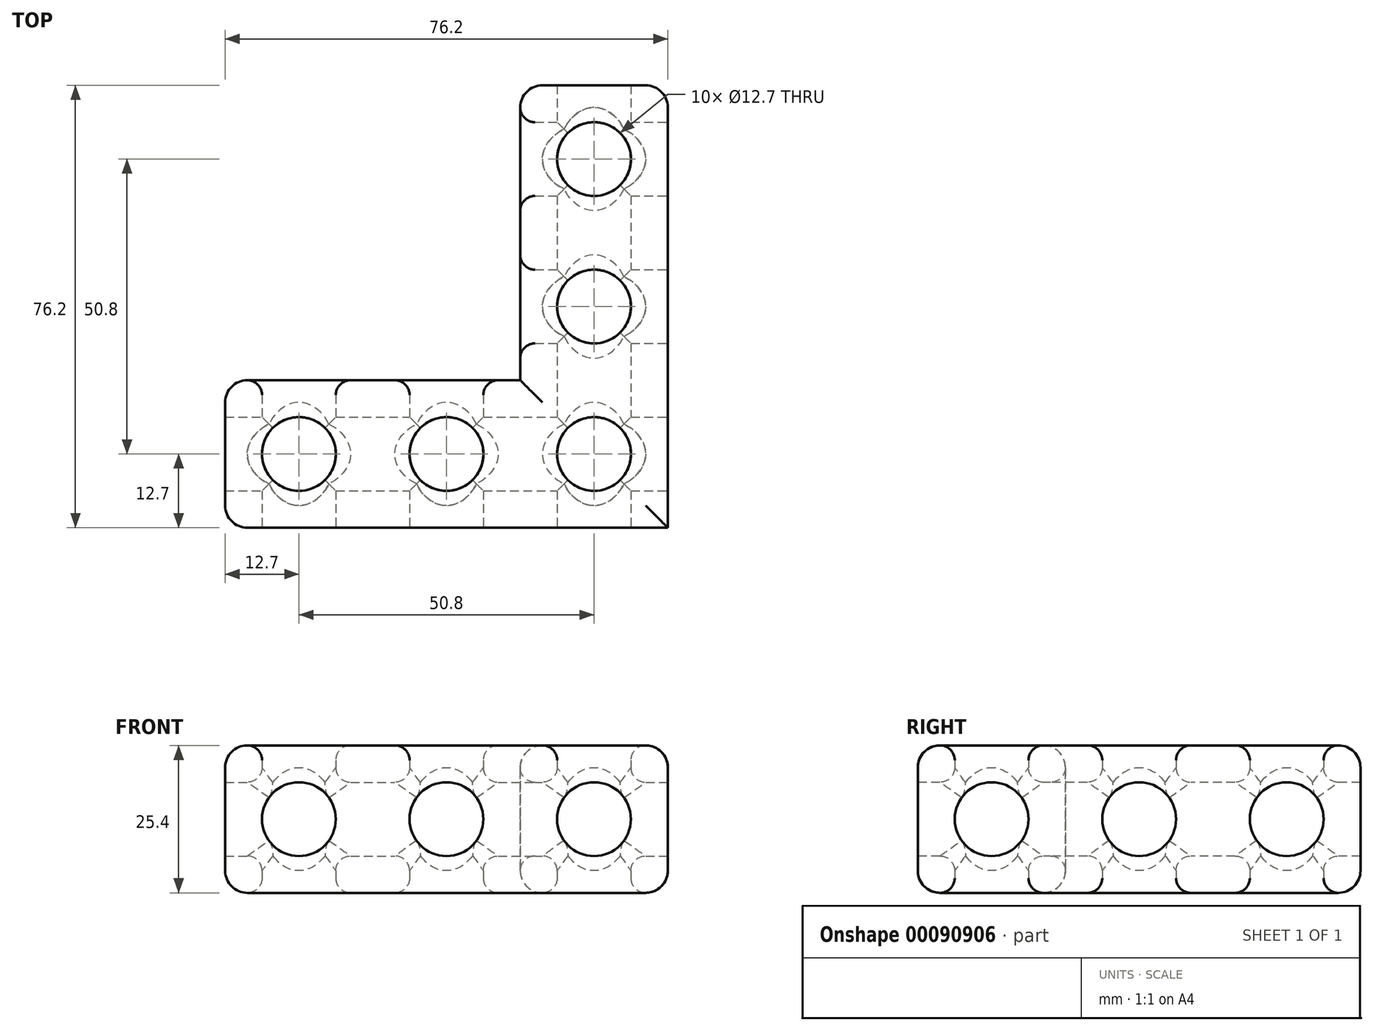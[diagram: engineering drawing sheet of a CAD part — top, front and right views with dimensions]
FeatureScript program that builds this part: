
annotation { "Feature Type Name" : "Feature", "Feature Type Description" : "" }
export const myFeature = defineFeature(function(context is Context, id is Id, definition is map)
    precondition{}
    {
        {
            var Q0;
            Q0=qCreatedBy(makeId("Top.planeOp"),FACE);
            var sketch = newSketch(context, id + "F0", { "sketchPlane" : qUnion([Q0])});
            skLineSegment(sketch, "E0.bottom", {"start": v(0, 0) * mm, "end": v(76.2, 0) * mm});
            skLineSegment(sketch, "E0.left", {"start": v(0, 0) * mm, "end": v(0, 25.4) * mm});
            skLineSegment(sketch, "E0.right", {"start": v(76.2, 0) * mm, "end": v(76.2, 18.8) * mm});
            skLineSegment(sketch, "E1.bottom", {"start": v(76.2, 0) * mm, "end": v(57.4, 0) * mm});
            skLineSegment(sketch, "E1.top", {"start": v(76.2, 76.2) * mm, "end": v(50.8, 76.2) * mm});
            skLineSegment(sketch, "E1.left", {"start": v(76.2, 0) * mm, "end": v(76.2, 76.2) * mm});
            skLineSegment(sketch, "E2", {"start": v(50.8, 76.2) * mm, "end": v(50.8, 25.4) * mm});
            skLineSegment(sketch, "E3", {"start": v(0, 25.4) * mm, "end": v(50.8, 25.4) * mm});
            skCircle(sketch, "E4", {"center": v(12.7, 12.7) * mm, "radius": 6.35 * mm});
            skCircle(sketch, "E5", {"center": v(38.1, 12.7) * mm, "radius": 6.35 * mm});
            skCircle(sketch, "E6", {"center": v(63.5, 12.7) * mm, "radius": 6.35 * mm});
            skCircle(sketch, "E7", {"center": v(63.5, 38.1) * mm, "radius": 6.35 * mm});
            skCircle(sketch, "E8", {"center": v(63.5, 63.5) * mm, "radius": 6.35 * mm});
            skSolve(sketch);
        }
        {
            var Q0;
            Q0 = qSketchRegion(id + "F0", true);
            extrude(context, id + "F1", {"entities" : qUnion([Q0]), "depth" : 25.4 * mm});
        }
        {
            var Q0;
            Q0=makeQuery(id+"F1.opExtrude","SWEPT_FACE",FACE,{"disambiguationData":[OSD([sQuery(id+"F0.wireOp",EDGE,"E0.bottom"),sQuery(id+"F0.wireOp",EDGE,"E1.bottom")])]});
            var sketch = newSketch(context, id + "F2", { "sketchPlane" : qUnion([Q0])});
            skCircle(sketch, "E9", {"center": v(12.7, 12.7) * mm, "radius": 6.35 * mm});
            skCircle(sketch, "E10", {"center": v(38.1, 12.7) * mm, "radius": 6.35 * mm});
            skCircle(sketch, "E11", {"center": v(63.5, 12.7) * mm, "radius": 6.35 * mm});
            skSolve(sketch);
        }
        {
            var Q0;
            Q0 = qSketchRegion(id + "F2", true);
            extrude(context, id + "F3", {"entities" : qUnion([Q0]), "operationType" : NewBodyOperationType.REMOVE, "oppositeDirection" : true, "depth" : 76.2 * mm});
        }
        {
            var Q0;
            Q0=makeQuery(id+"F1.opExtrude","SWEPT_FACE",FACE,{"disambiguationData":[OSD([sQuery(id+"F0.wireOp",EDGE,"E1.left")])]});
            var sketch = newSketch(context, id + "F4", { "sketchPlane" : qUnion([Q0])});
            skLineSegment(sketch, "E12.bottom", {"start": v(0, 0) * mm, "end": v(25.4, 0) * mm});
            skLineSegment(sketch, "E12.top", {"start": v(0, 25.4) * mm, "end": v(25.4, 25.4) * mm});
            skLineSegment(sketch, "E12.left", {"start": v(0, 0) * mm, "end": v(0, 25.4) * mm});
            skLineSegment(sketch, "E13.bottom", {"start": v(25.4, 0) * mm, "end": v(50.8, 0) * mm});
            skLineSegment(sketch, "E13.top", {"start": v(25.4, 25.4) * mm, "end": v(50.8, 25.4) * mm});
            skLineSegment(sketch, "E14.bottom", {"start": v(50.8, 0) * mm, "end": v(76.2, 0) * mm});
            skLineSegment(sketch, "E14.top", {"start": v(50.8, 25.4) * mm, "end": v(76.2, 25.4) * mm});
            skLineSegment(sketch, "E14.right", {"start": v(76.2, 0) * mm, "end": v(76.2, 25.4) * mm});
            skCircle(sketch, "E15", {"center": v(12.7, 12.7) * mm, "radius": 6.35 * mm});
            skCircle(sketch, "E16", {"center": v(38.1, 12.7) * mm, "radius": 6.35 * mm});
            skCircle(sketch, "E17", {"center": v(63.5, 12.7) * mm, "radius": 6.35 * mm});
            skSolve(sketch);
        }
        {
            var Q0;
            Q0=makeQuery(id+"F4.imprint","IMPRINT",FACE,{"disambiguationData":[TD([[makeQuery(id+"F4.imprint","IMPRINT",EDGE,{"derivedFrom":sQuery(id+"F4.wireOp",EDGE,"E15")}),1.0]])]});
            var Q1;
            Q1=makeQuery(id+"F4.imprint","IMPRINT",FACE,{"disambiguationData":[TD([[makeQuery(id+"F4.imprint","IMPRINT",EDGE,{"derivedFrom":sQuery(id+"F4.wireOp",EDGE,"E16")}),1.0]])]});
            var Q2;
            Q2=makeQuery(id+"F4.imprint","IMPRINT",FACE,{"disambiguationData":[TD([[makeQuery(id+"F4.imprint","IMPRINT",EDGE,{"derivedFrom":sQuery(id+"F4.wireOp",EDGE,"E17")}),1.0]])]});
            extrude(context, id + "F5", {"entities" : qUnion([Q0, Q1, Q2]), "operationType" : NewBodyOperationType.REMOVE, "oppositeDirection" : true, "depth" : 76.2 * mm});
        }
        {
            var Q0;
            Q0=makeQuery(id+"F1.opExtrude","CAP_EDGE",EDGE,{"disambiguationData":[OSD([sQuery(id+"F0.wireOp",EDGE,"E0.bottom"),sQuery(id+"F0.wireOp",EDGE,"E1.bottom")])],"isStart":false});
            var Q1;
            Q1=makeQuery(id+"F1.opExtrude","CAP_EDGE",EDGE,{"disambiguationData":[OSD([sQuery(id+"F0.wireOp",EDGE,"E1.left")])],"isStart":false});
            var Q2;
            Q2=makeQuery(id+"F1.opExtrude","CAP_EDGE",EDGE,{"disambiguationData":[OSD([sQuery(id+"F0.wireOp",EDGE,"E3")])],"isStart":false});
            var Q3;
            Q3=makeQuery(id+"F1.opExtrude","CAP_EDGE",EDGE,{"disambiguationData":[OSD([sQuery(id+"F0.wireOp",EDGE,"E2")])],"isStart":false});
            var Q4;
            Q4=makeQuery(id+"F1.opExtrude","SWEPT_EDGE",EDGE,{"disambiguationData":[OSD([sQuery(id+"F0.wireOp",EDGE,"E0.bottom"),sQuery(id+"F0.wireOp",EDGE,"E0.left")])]});
            var Q5;
            Q5=makeQuery(id+"F1.opExtrude","CAP_EDGE",EDGE,{"disambiguationData":[OSD([sQuery(id+"F0.wireOp",EDGE,"E0.bottom"),sQuery(id+"F0.wireOp",EDGE,"E1.bottom")])],"isStart":true});
            var Q6;
            Q6=makeQuery(id+"F1.opExtrude","CAP_EDGE",EDGE,{"disambiguationData":[OSD([sQuery(id+"F0.wireOp",EDGE,"E1.left")])],"isStart":true});
            var Q7;
            Q7=makeQuery(id+"F1.opExtrude","SWEPT_EDGE",EDGE,{"disambiguationData":[OSD([sQuery(id+"F0.wireOp",EDGE,"E1.bottom"),sQuery(id+"F0.wireOp",EDGE,"E1.left")])]});
            var Q8;
            Q8=makeQuery(id+"F1.opExtrude","CAP_EDGE",EDGE,{"disambiguationData":[OSD([sQuery(id+"F0.wireOp",EDGE,"E0.left")])],"isStart":false});
            var Q9;
            Q9=makeQuery(id+"F1.opExtrude","CAP_EDGE",EDGE,{"disambiguationData":[OSD([sQuery(id+"F0.wireOp",EDGE,"E0.left")])],"isStart":true});
            var Q10;
            Q10=makeQuery(id+"F1.opExtrude","SWEPT_EDGE",EDGE,{"disambiguationData":[OSD([sQuery(id+"F0.wireOp",EDGE,"E0.left"),sQuery(id+"F0.wireOp",EDGE,"E3")])]});
            var Q11;
            Q11=makeQuery(id+"F1.opExtrude","CAP_EDGE",EDGE,{"disambiguationData":[OSD([sQuery(id+"F0.wireOp",EDGE,"E3")])],"isStart":true});
            var Q12;
            Q12=makeQuery(id+"F1.opExtrude","SWEPT_EDGE",EDGE,{"disambiguationData":[OSD([sQuery(id+"F0.wireOp",EDGE,"E1.top"),sQuery(id+"F0.wireOp",EDGE,"E2")])]});
            var Q13;
            Q13=makeQuery(id+"F1.opExtrude","CAP_EDGE",EDGE,{"disambiguationData":[OSD([sQuery(id+"F0.wireOp",EDGE,"E2")])],"isStart":true});
            var Q14;
            Q14=makeQuery(id+"F1.opExtrude","CAP_EDGE",EDGE,{"disambiguationData":[OSD([sQuery(id+"F0.wireOp",EDGE,"E1.top")])],"isStart":true});
            var Q15;
            Q15=makeQuery(id+"F1.opExtrude","SWEPT_EDGE",EDGE,{"disambiguationData":[OSD([sQuery(id+"F0.wireOp",EDGE,"E1.top"),sQuery(id+"F0.wireOp",EDGE,"E1.left")])]});
            var Q16;
            Q16=makeQuery(id+"F1.opExtrude","CAP_EDGE",EDGE,{"disambiguationData":[OSD([sQuery(id+"F0.wireOp",EDGE,"E1.top")])],"isStart":false});
            fillet(context, id + "F6", {"entities" : qUnion([Q0, Q1, Q2, Q3, Q4, Q5, Q6, Q7, Q8, Q9, Q10, Q11, Q12, Q13, Q14, Q15, Q16]), "radius" : 3.8 * mm, "allowEdgeOverflow" : false});
        }
        {
            var Q0;
            {var subQ0=sQuery(id+"F0.wireOp",EDGE,"E4");var subQ1=makeQuery(id+"F1.opExtrude","SWEPT_FACE",FACE,{"disambiguationData":[OSD([subQ0])]});Q0=makeQuery(id+"F5.boolean.opBoolean","INTERSECT",EDGE,{"disambiguationData":[OD(0.0)],"derivedFrom":[makeQuery(id+"F3.boolean.opBoolean","SPLIT",FACE,{"disambiguationData":[TD([makeQuery(id+"F1.opExtrude","CAP_FACE",FACE,{"disambiguationData":[OSD([sQuery(id+"F0.wireOp",EDGE,"E0.bottom"),sQuery(id+"F0.wireOp",EDGE,"E0.left"),sQuery(id+"F0.wireOp",EDGE,"E1.bottom"),sQuery(id+"F0.wireOp",EDGE,"E1.top"),sQuery(id+"F0.wireOp",EDGE,"E1.left"),sQuery(id+"F0.wireOp",EDGE,"E2"),sQuery(id+"F0.wireOp",EDGE,"E3"),subQ0,sQuery(id+"F0.wireOp",EDGE,"E5"),sQuery(id+"F0.wireOp",EDGE,"E6"),sQuery(id+"F0.wireOp",EDGE,"E7"),sQuery(id+"F0.wireOp",EDGE,"E8")])],"isStart":true})])],"derivedFrom":subQ1}),makeQuery(id+"F5.opExtrude","SWEPT_FACE",FACE,{"disambiguationData":[OSD([sQuery(id+"F4.wireOp",EDGE,"E15")])]})]});}
            var Q1;
            Q1=makeQuery(id+"F3.boolean.opBoolean","INTERSECT",EDGE,{"disambiguationData":[OD(0.0)],"derivedFrom":[makeQuery(id+"F1.opExtrude","SWEPT_FACE",FACE,{"disambiguationData":[OSD([sQuery(id+"F0.wireOp",EDGE,"E4")])]}),makeQuery(id+"F3.opExtrude","SWEPT_FACE",FACE,{"disambiguationData":[OSD([sQuery(id+"F2.wireOp",EDGE,"E9")])]})]});
            var Q2;
            Q2=makeQuery(id+"F5.boolean.opBoolean","INTERSECT",EDGE,{"disambiguationData":[OD(0.0)],"derivedFrom":[makeQuery(id+"F3.boolean.opBoolean","COPY",FACE,{"disambiguationData":[OD(0.0)],"derivedFrom":makeQuery(id+"F3.opExtrude","SWEPT_FACE",FACE,{"disambiguationData":[OSD([sQuery(id+"F2.wireOp",EDGE,"E9")])]})}),makeQuery(id+"F5.opExtrude","SWEPT_FACE",FACE,{"disambiguationData":[OSD([sQuery(id+"F4.wireOp",EDGE,"E15")])]})]});
            var Q3;
            Q3=makeQuery(id+"F5.boolean.opBoolean","INTERSECT",EDGE,{"disambiguationData":[OD(0.0)],"derivedFrom":[makeQuery(id+"F3.boolean.opBoolean","COPY",FACE,{"disambiguationData":[OD(1.0)],"derivedFrom":makeQuery(id+"F3.opExtrude","SWEPT_FACE",FACE,{"disambiguationData":[OSD([sQuery(id+"F2.wireOp",EDGE,"E9")])]})}),makeQuery(id+"F5.opExtrude","SWEPT_FACE",FACE,{"disambiguationData":[OSD([sQuery(id+"F4.wireOp",EDGE,"E15")])]})]});
            var Q4;
            {var subQ0=sQuery(id+"F0.wireOp",EDGE,"E4");var subQ1=makeQuery(id+"F1.opExtrude","SWEPT_FACE",FACE,{"disambiguationData":[OSD([subQ0])]});Q4=makeQuery(id+"F5.boolean.opBoolean","INTERSECT",EDGE,{"disambiguationData":[OD(0.0)],"derivedFrom":[makeQuery(id+"F3.boolean.opBoolean","SPLIT",FACE,{"disambiguationData":[TD([makeQuery(id+"F1.opExtrude","CAP_FACE",FACE,{"disambiguationData":[OSD([sQuery(id+"F0.wireOp",EDGE,"E0.bottom"),sQuery(id+"F0.wireOp",EDGE,"E0.left"),sQuery(id+"F0.wireOp",EDGE,"E1.bottom"),sQuery(id+"F0.wireOp",EDGE,"E1.top"),sQuery(id+"F0.wireOp",EDGE,"E1.left"),sQuery(id+"F0.wireOp",EDGE,"E2"),sQuery(id+"F0.wireOp",EDGE,"E3"),subQ0,sQuery(id+"F0.wireOp",EDGE,"E5"),sQuery(id+"F0.wireOp",EDGE,"E6"),sQuery(id+"F0.wireOp",EDGE,"E7"),sQuery(id+"F0.wireOp",EDGE,"E8")])],"isStart":false})])],"derivedFrom":subQ1}),makeQuery(id+"F5.opExtrude","SWEPT_FACE",FACE,{"disambiguationData":[OSD([sQuery(id+"F4.wireOp",EDGE,"E15")])]})]});}
            var Q5;
            Q5=makeQuery(id+"F3.boolean.opBoolean","INTERSECT",EDGE,{"disambiguationData":[OD(3.0)],"derivedFrom":[makeQuery(id+"F1.opExtrude","SWEPT_FACE",FACE,{"disambiguationData":[OSD([sQuery(id+"F0.wireOp",EDGE,"E4")])]}),makeQuery(id+"F3.opExtrude","SWEPT_FACE",FACE,{"disambiguationData":[OSD([sQuery(id+"F2.wireOp",EDGE,"E9")])]})]});
            var Q6;
            Q6=makeQuery(id+"F3.boolean.opBoolean","INTERSECT",EDGE,{"disambiguationData":[OD(1.0)],"derivedFrom":[makeQuery(id+"F1.opExtrude","SWEPT_FACE",FACE,{"disambiguationData":[OSD([sQuery(id+"F0.wireOp",EDGE,"E4")])]}),makeQuery(id+"F3.opExtrude","SWEPT_FACE",FACE,{"disambiguationData":[OSD([sQuery(id+"F2.wireOp",EDGE,"E9")])]})]});
            var Q7;
            {var subQ0=sQuery(id+"F0.wireOp",EDGE,"E4");var subQ1=makeQuery(id+"F1.opExtrude","SWEPT_FACE",FACE,{"disambiguationData":[OSD([subQ0])]});Q7=makeQuery(id+"F5.boolean.opBoolean","INTERSECT",EDGE,{"disambiguationData":[OD(1.0)],"derivedFrom":[makeQuery(id+"F3.boolean.opBoolean","SPLIT",FACE,{"disambiguationData":[TD([makeQuery(id+"F1.opExtrude","CAP_FACE",FACE,{"disambiguationData":[OSD([sQuery(id+"F0.wireOp",EDGE,"E0.bottom"),sQuery(id+"F0.wireOp",EDGE,"E0.left"),sQuery(id+"F0.wireOp",EDGE,"E1.bottom"),sQuery(id+"F0.wireOp",EDGE,"E1.top"),sQuery(id+"F0.wireOp",EDGE,"E1.left"),sQuery(id+"F0.wireOp",EDGE,"E2"),sQuery(id+"F0.wireOp",EDGE,"E3"),subQ0,sQuery(id+"F0.wireOp",EDGE,"E5"),sQuery(id+"F0.wireOp",EDGE,"E6"),sQuery(id+"F0.wireOp",EDGE,"E7"),sQuery(id+"F0.wireOp",EDGE,"E8")])],"isStart":true})])],"derivedFrom":subQ1}),makeQuery(id+"F5.opExtrude","SWEPT_FACE",FACE,{"disambiguationData":[OSD([sQuery(id+"F4.wireOp",EDGE,"E15")])]})]});}
            var Q8;
            Q8=makeQuery(id+"F5.boolean.opBoolean","INTERSECT",EDGE,{"disambiguationData":[OD(1.0)],"derivedFrom":[makeQuery(id+"F3.boolean.opBoolean","COPY",FACE,{"disambiguationData":[OD(0.0)],"derivedFrom":makeQuery(id+"F3.opExtrude","SWEPT_FACE",FACE,{"disambiguationData":[OSD([sQuery(id+"F2.wireOp",EDGE,"E9")])]})}),makeQuery(id+"F5.opExtrude","SWEPT_FACE",FACE,{"disambiguationData":[OSD([sQuery(id+"F4.wireOp",EDGE,"E15")])]})]});
            var Q9;
            Q9=makeQuery(id+"F3.boolean.opBoolean","INTERSECT",EDGE,{"disambiguationData":[OD(2.0)],"derivedFrom":[makeQuery(id+"F1.opExtrude","SWEPT_FACE",FACE,{"disambiguationData":[OSD([sQuery(id+"F0.wireOp",EDGE,"E4")])]}),makeQuery(id+"F3.opExtrude","SWEPT_FACE",FACE,{"disambiguationData":[OSD([sQuery(id+"F2.wireOp",EDGE,"E9")])]})]});
            var Q10;
            {var subQ0=sQuery(id+"F0.wireOp",EDGE,"E4");var subQ1=makeQuery(id+"F1.opExtrude","SWEPT_FACE",FACE,{"disambiguationData":[OSD([subQ0])]});Q10=makeQuery(id+"F5.boolean.opBoolean","INTERSECT",EDGE,{"disambiguationData":[OD(1.0)],"derivedFrom":[makeQuery(id+"F3.boolean.opBoolean","SPLIT",FACE,{"disambiguationData":[TD([makeQuery(id+"F1.opExtrude","CAP_FACE",FACE,{"disambiguationData":[OSD([sQuery(id+"F0.wireOp",EDGE,"E0.bottom"),sQuery(id+"F0.wireOp",EDGE,"E0.left"),sQuery(id+"F0.wireOp",EDGE,"E1.bottom"),sQuery(id+"F0.wireOp",EDGE,"E1.top"),sQuery(id+"F0.wireOp",EDGE,"E1.left"),sQuery(id+"F0.wireOp",EDGE,"E2"),sQuery(id+"F0.wireOp",EDGE,"E3"),subQ0,sQuery(id+"F0.wireOp",EDGE,"E5"),sQuery(id+"F0.wireOp",EDGE,"E6"),sQuery(id+"F0.wireOp",EDGE,"E7"),sQuery(id+"F0.wireOp",EDGE,"E8")])],"isStart":false})])],"derivedFrom":subQ1}),makeQuery(id+"F5.opExtrude","SWEPT_FACE",FACE,{"disambiguationData":[OSD([sQuery(id+"F4.wireOp",EDGE,"E15")])]})]});}
            var Q11;
            Q11=makeQuery(id+"F5.boolean.opBoolean","INTERSECT",EDGE,{"disambiguationData":[OD(1.0)],"derivedFrom":[makeQuery(id+"F3.boolean.opBoolean","COPY",FACE,{"disambiguationData":[OD(1.0)],"derivedFrom":makeQuery(id+"F3.opExtrude","SWEPT_FACE",FACE,{"disambiguationData":[OSD([sQuery(id+"F2.wireOp",EDGE,"E9")])]})}),makeQuery(id+"F5.opExtrude","SWEPT_FACE",FACE,{"disambiguationData":[OSD([sQuery(id+"F4.wireOp",EDGE,"E15")])]})]});
            fillet(context, id + "F7", {"entities" : qUnion([Q0, Q1, Q2, Q3, Q4, Q5, Q6, Q7, Q8, Q9, Q10, Q11]), "radius" : 2.54 * mm, "tangentPropagation" : true, "allowEdgeOverflow" : false});
        }
        {
            var Q0;
            {var subQ0=sQuery(id+"F0.wireOp",EDGE,"E5");var subQ1=makeQuery(id+"F1.opExtrude","SWEPT_FACE",FACE,{"disambiguationData":[OSD([subQ0])]});Q0=makeQuery(id+"F5.boolean.opBoolean","INTERSECT",EDGE,{"disambiguationData":[OD(0.0)],"derivedFrom":[makeQuery(id+"F3.boolean.opBoolean","SPLIT",FACE,{"disambiguationData":[TD([makeQuery(id+"F1.opExtrude","CAP_FACE",FACE,{"disambiguationData":[OSD([sQuery(id+"F0.wireOp",EDGE,"E0.bottom"),sQuery(id+"F0.wireOp",EDGE,"E0.left"),sQuery(id+"F0.wireOp",EDGE,"E1.bottom"),sQuery(id+"F0.wireOp",EDGE,"E1.top"),sQuery(id+"F0.wireOp",EDGE,"E1.left"),sQuery(id+"F0.wireOp",EDGE,"E2"),sQuery(id+"F0.wireOp",EDGE,"E3"),sQuery(id+"F0.wireOp",EDGE,"E4"),subQ0,sQuery(id+"F0.wireOp",EDGE,"E6"),sQuery(id+"F0.wireOp",EDGE,"E7"),sQuery(id+"F0.wireOp",EDGE,"E8")])],"isStart":true})])],"derivedFrom":subQ1}),makeQuery(id+"F5.opExtrude","SWEPT_FACE",FACE,{"disambiguationData":[OSD([sQuery(id+"F4.wireOp",EDGE,"E15")])]})]});}
            var Q1;
            Q1=makeQuery(id+"F3.boolean.opBoolean","INTERSECT",EDGE,{"disambiguationData":[OD(0.0)],"derivedFrom":[makeQuery(id+"F1.opExtrude","SWEPT_FACE",FACE,{"disambiguationData":[OSD([sQuery(id+"F0.wireOp",EDGE,"E5")])]}),makeQuery(id+"F3.opExtrude","SWEPT_FACE",FACE,{"disambiguationData":[OSD([sQuery(id+"F2.wireOp",EDGE,"E10")])]})]});
            var Q2;
            Q2=makeQuery(id+"F3.boolean.opBoolean","INTERSECT",EDGE,{"disambiguationData":[OD(1.0)],"derivedFrom":[makeQuery(id+"F1.opExtrude","SWEPT_FACE",FACE,{"disambiguationData":[OSD([sQuery(id+"F0.wireOp",EDGE,"E5")])]}),makeQuery(id+"F3.opExtrude","SWEPT_FACE",FACE,{"disambiguationData":[OSD([sQuery(id+"F2.wireOp",EDGE,"E10")])]})]});
            var Q3;
            {var subQ0=sQuery(id+"F0.wireOp",EDGE,"E5");var subQ1=makeQuery(id+"F1.opExtrude","SWEPT_FACE",FACE,{"disambiguationData":[OSD([subQ0])]});Q3=makeQuery(id+"F5.boolean.opBoolean","INTERSECT",EDGE,{"disambiguationData":[OD(1.0)],"derivedFrom":[makeQuery(id+"F3.boolean.opBoolean","SPLIT",FACE,{"disambiguationData":[TD([makeQuery(id+"F1.opExtrude","CAP_FACE",FACE,{"disambiguationData":[OSD([sQuery(id+"F0.wireOp",EDGE,"E0.bottom"),sQuery(id+"F0.wireOp",EDGE,"E0.left"),sQuery(id+"F0.wireOp",EDGE,"E1.bottom"),sQuery(id+"F0.wireOp",EDGE,"E1.top"),sQuery(id+"F0.wireOp",EDGE,"E1.left"),sQuery(id+"F0.wireOp",EDGE,"E2"),sQuery(id+"F0.wireOp",EDGE,"E3"),sQuery(id+"F0.wireOp",EDGE,"E4"),subQ0,sQuery(id+"F0.wireOp",EDGE,"E6"),sQuery(id+"F0.wireOp",EDGE,"E7"),sQuery(id+"F0.wireOp",EDGE,"E8")])],"isStart":true})])],"derivedFrom":subQ1}),makeQuery(id+"F5.opExtrude","SWEPT_FACE",FACE,{"disambiguationData":[OSD([sQuery(id+"F4.wireOp",EDGE,"E15")])]})]});}
            var Q4;
            Q4=makeQuery(id+"F5.boolean.opBoolean","INTERSECT",EDGE,{"disambiguationData":[OD(0.0)],"derivedFrom":[makeQuery(id+"F3.boolean.opBoolean","COPY",FACE,{"disambiguationData":[OD(0.0)],"derivedFrom":makeQuery(id+"F3.opExtrude","SWEPT_FACE",FACE,{"disambiguationData":[OSD([sQuery(id+"F2.wireOp",EDGE,"E10")])]})}),makeQuery(id+"F5.opExtrude","SWEPT_FACE",FACE,{"disambiguationData":[OSD([sQuery(id+"F4.wireOp",EDGE,"E15")])]})]});
            var Q5;
            Q5=makeQuery(id+"F5.boolean.opBoolean","INTERSECT",EDGE,{"disambiguationData":[OD(0.0)],"derivedFrom":[makeQuery(id+"F3.boolean.opBoolean","COPY",FACE,{"disambiguationData":[OD(1.0)],"derivedFrom":makeQuery(id+"F3.opExtrude","SWEPT_FACE",FACE,{"disambiguationData":[OSD([sQuery(id+"F2.wireOp",EDGE,"E10")])]})}),makeQuery(id+"F5.opExtrude","SWEPT_FACE",FACE,{"disambiguationData":[OSD([sQuery(id+"F4.wireOp",EDGE,"E15")])]})]});
            var Q6;
            Q6=makeQuery(id+"F5.boolean.opBoolean","INTERSECT",EDGE,{"disambiguationData":[OD(1.0)],"derivedFrom":[makeQuery(id+"F3.boolean.opBoolean","COPY",FACE,{"disambiguationData":[OD(1.0)],"derivedFrom":makeQuery(id+"F3.opExtrude","SWEPT_FACE",FACE,{"disambiguationData":[OSD([sQuery(id+"F2.wireOp",EDGE,"E10")])]})}),makeQuery(id+"F5.opExtrude","SWEPT_FACE",FACE,{"disambiguationData":[OSD([sQuery(id+"F4.wireOp",EDGE,"E15")])]})]});
            var Q7;
            Q7=makeQuery(id+"F5.boolean.opBoolean","INTERSECT",EDGE,{"disambiguationData":[OD(1.0)],"derivedFrom":[makeQuery(id+"F3.boolean.opBoolean","COPY",FACE,{"disambiguationData":[OD(0.0)],"derivedFrom":makeQuery(id+"F3.opExtrude","SWEPT_FACE",FACE,{"disambiguationData":[OSD([sQuery(id+"F2.wireOp",EDGE,"E10")])]})}),makeQuery(id+"F5.opExtrude","SWEPT_FACE",FACE,{"disambiguationData":[OSD([sQuery(id+"F4.wireOp",EDGE,"E15")])]})]});
            var Q8;
            Q8=makeQuery(id+"F3.boolean.opBoolean","INTERSECT",EDGE,{"disambiguationData":[OD(2.0)],"derivedFrom":[makeQuery(id+"F1.opExtrude","SWEPT_FACE",FACE,{"disambiguationData":[OSD([sQuery(id+"F0.wireOp",EDGE,"E5")])]}),makeQuery(id+"F3.opExtrude","SWEPT_FACE",FACE,{"disambiguationData":[OSD([sQuery(id+"F2.wireOp",EDGE,"E10")])]})]});
            var Q9;
            {var subQ0=sQuery(id+"F0.wireOp",EDGE,"E5");var subQ1=makeQuery(id+"F1.opExtrude","SWEPT_FACE",FACE,{"disambiguationData":[OSD([subQ0])]});Q9=makeQuery(id+"F5.boolean.opBoolean","INTERSECT",EDGE,{"disambiguationData":[OD(0.0)],"derivedFrom":[makeQuery(id+"F3.boolean.opBoolean","SPLIT",FACE,{"disambiguationData":[TD([makeQuery(id+"F1.opExtrude","CAP_FACE",FACE,{"disambiguationData":[OSD([sQuery(id+"F0.wireOp",EDGE,"E0.bottom"),sQuery(id+"F0.wireOp",EDGE,"E0.left"),sQuery(id+"F0.wireOp",EDGE,"E1.bottom"),sQuery(id+"F0.wireOp",EDGE,"E1.top"),sQuery(id+"F0.wireOp",EDGE,"E1.left"),sQuery(id+"F0.wireOp",EDGE,"E2"),sQuery(id+"F0.wireOp",EDGE,"E3"),sQuery(id+"F0.wireOp",EDGE,"E4"),subQ0,sQuery(id+"F0.wireOp",EDGE,"E6"),sQuery(id+"F0.wireOp",EDGE,"E7"),sQuery(id+"F0.wireOp",EDGE,"E8")])],"isStart":false})])],"derivedFrom":subQ1}),makeQuery(id+"F5.opExtrude","SWEPT_FACE",FACE,{"disambiguationData":[OSD([sQuery(id+"F4.wireOp",EDGE,"E15")])]})]});}
            var Q10;
            Q10=makeQuery(id+"F3.boolean.opBoolean","INTERSECT",EDGE,{"disambiguationData":[OD(3.0)],"derivedFrom":[makeQuery(id+"F1.opExtrude","SWEPT_FACE",FACE,{"disambiguationData":[OSD([sQuery(id+"F0.wireOp",EDGE,"E5")])]}),makeQuery(id+"F3.opExtrude","SWEPT_FACE",FACE,{"disambiguationData":[OSD([sQuery(id+"F2.wireOp",EDGE,"E10")])]})]});
            var Q11;
            {var subQ0=sQuery(id+"F0.wireOp",EDGE,"E5");var subQ1=makeQuery(id+"F1.opExtrude","SWEPT_FACE",FACE,{"disambiguationData":[OSD([subQ0])]});Q11=makeQuery(id+"F5.boolean.opBoolean","INTERSECT",EDGE,{"disambiguationData":[OD(1.0)],"derivedFrom":[makeQuery(id+"F3.boolean.opBoolean","SPLIT",FACE,{"disambiguationData":[TD([makeQuery(id+"F1.opExtrude","CAP_FACE",FACE,{"disambiguationData":[OSD([sQuery(id+"F0.wireOp",EDGE,"E0.bottom"),sQuery(id+"F0.wireOp",EDGE,"E0.left"),sQuery(id+"F0.wireOp",EDGE,"E1.bottom"),sQuery(id+"F0.wireOp",EDGE,"E1.top"),sQuery(id+"F0.wireOp",EDGE,"E1.left"),sQuery(id+"F0.wireOp",EDGE,"E2"),sQuery(id+"F0.wireOp",EDGE,"E3"),sQuery(id+"F0.wireOp",EDGE,"E4"),subQ0,sQuery(id+"F0.wireOp",EDGE,"E6"),sQuery(id+"F0.wireOp",EDGE,"E7"),sQuery(id+"F0.wireOp",EDGE,"E8")])],"isStart":false})])],"derivedFrom":subQ1}),makeQuery(id+"F5.opExtrude","SWEPT_FACE",FACE,{"disambiguationData":[OSD([sQuery(id+"F4.wireOp",EDGE,"E15")])]})]});}
            var Q12;
            Q12=makeQuery(id+"F5.boolean.opBoolean","INTERSECT",EDGE,{"disambiguationData":[OD(1.0)],"derivedFrom":[makeQuery(id+"F3.boolean.opBoolean","COPY",FACE,{"disambiguationData":[OD(2.0)],"derivedFrom":makeQuery(id+"F3.opExtrude","SWEPT_FACE",FACE,{"disambiguationData":[OSD([sQuery(id+"F2.wireOp",EDGE,"E11")])]})}),makeQuery(id+"F5.opExtrude","SWEPT_FACE",FACE,{"disambiguationData":[OSD([sQuery(id+"F4.wireOp",EDGE,"E15")])]})]});
            var Q13;
            {var subQ0=sQuery(id+"F0.wireOp",EDGE,"E6");var subQ1=makeQuery(id+"F1.opExtrude","SWEPT_FACE",FACE,{"disambiguationData":[OSD([subQ0])]});Q13=makeQuery(id+"F5.boolean.opBoolean","INTERSECT",EDGE,{"disambiguationData":[OD(1.0)],"derivedFrom":[makeQuery(id+"F3.boolean.opBoolean","SPLIT",FACE,{"disambiguationData":[TD([makeQuery(id+"F1.opExtrude","CAP_FACE",FACE,{"disambiguationData":[OSD([sQuery(id+"F0.wireOp",EDGE,"E0.bottom"),sQuery(id+"F0.wireOp",EDGE,"E0.left"),sQuery(id+"F0.wireOp",EDGE,"E1.bottom"),sQuery(id+"F0.wireOp",EDGE,"E1.top"),sQuery(id+"F0.wireOp",EDGE,"E1.left"),sQuery(id+"F0.wireOp",EDGE,"E2"),sQuery(id+"F0.wireOp",EDGE,"E3"),sQuery(id+"F0.wireOp",EDGE,"E4"),sQuery(id+"F0.wireOp",EDGE,"E5"),subQ0,sQuery(id+"F0.wireOp",EDGE,"E7"),sQuery(id+"F0.wireOp",EDGE,"E8")])],"isStart":true})])],"derivedFrom":subQ1}),makeQuery(id+"F5.opExtrude","SWEPT_FACE",FACE,{"disambiguationData":[OSD([sQuery(id+"F4.wireOp",EDGE,"E15")])]})]});}
            var Q14;
            Q14=makeQuery(id+"F3.boolean.opBoolean","INTERSECT",EDGE,{"disambiguationData":[OD(2.0)],"derivedFrom":[makeQuery(id+"F1.opExtrude","SWEPT_FACE",FACE,{"disambiguationData":[OSD([sQuery(id+"F0.wireOp",EDGE,"E6")])]}),makeQuery(id+"F3.opExtrude","SWEPT_FACE",FACE,{"disambiguationData":[OSD([sQuery(id+"F2.wireOp",EDGE,"E11")])]})]});
            var Q15;
            {var subQ0=sQuery(id+"F0.wireOp",EDGE,"E6");var subQ1=makeQuery(id+"F1.opExtrude","SWEPT_FACE",FACE,{"disambiguationData":[OSD([subQ0])]});Q15=makeQuery(id+"F5.boolean.opBoolean","INTERSECT",EDGE,{"disambiguationData":[OD(1.0)],"derivedFrom":[makeQuery(id+"F3.boolean.opBoolean","SPLIT",FACE,{"disambiguationData":[TD([makeQuery(id+"F1.opExtrude","CAP_FACE",FACE,{"disambiguationData":[OSD([sQuery(id+"F0.wireOp",EDGE,"E0.bottom"),sQuery(id+"F0.wireOp",EDGE,"E0.left"),sQuery(id+"F0.wireOp",EDGE,"E1.bottom"),sQuery(id+"F0.wireOp",EDGE,"E1.top"),sQuery(id+"F0.wireOp",EDGE,"E1.left"),sQuery(id+"F0.wireOp",EDGE,"E2"),sQuery(id+"F0.wireOp",EDGE,"E3"),sQuery(id+"F0.wireOp",EDGE,"E4"),sQuery(id+"F0.wireOp",EDGE,"E5"),subQ0,sQuery(id+"F0.wireOp",EDGE,"E7"),sQuery(id+"F0.wireOp",EDGE,"E8")])],"isStart":false})])],"derivedFrom":subQ1}),makeQuery(id+"F5.opExtrude","SWEPT_FACE",FACE,{"disambiguationData":[OSD([sQuery(id+"F4.wireOp",EDGE,"E15")])]})]});}
            var Q16;
            Q16=makeQuery(id+"F3.boolean.opBoolean","INTERSECT",EDGE,{"disambiguationData":[OD(3.0)],"derivedFrom":[makeQuery(id+"F1.opExtrude","SWEPT_FACE",FACE,{"disambiguationData":[OSD([sQuery(id+"F0.wireOp",EDGE,"E6")])]}),makeQuery(id+"F3.opExtrude","SWEPT_FACE",FACE,{"disambiguationData":[OSD([sQuery(id+"F2.wireOp",EDGE,"E11")])]})]});
            var Q17;
            Q17=makeQuery(id+"F3.boolean.opBoolean","INTERSECT",EDGE,{"disambiguationData":[OD(0.0)],"derivedFrom":[makeQuery(id+"F1.opExtrude","SWEPT_FACE",FACE,{"disambiguationData":[OSD([sQuery(id+"F0.wireOp",EDGE,"E6")])]}),makeQuery(id+"F3.opExtrude","SWEPT_FACE",FACE,{"disambiguationData":[OSD([sQuery(id+"F2.wireOp",EDGE,"E11")])]})]});
            var Q18;
            Q18=makeQuery(id+"F5.boolean.opBoolean","INTERSECT",EDGE,{"disambiguationData":[OD(0.0)],"derivedFrom":[makeQuery(id+"F3.boolean.opBoolean","COPY",FACE,{"disambiguationData":[OD(0.0)],"derivedFrom":makeQuery(id+"F3.opExtrude","SWEPT_FACE",FACE,{"disambiguationData":[OSD([sQuery(id+"F2.wireOp",EDGE,"E11")])]})}),makeQuery(id+"F5.opExtrude","SWEPT_FACE",FACE,{"disambiguationData":[OSD([sQuery(id+"F4.wireOp",EDGE,"E15")])]})]});
            var Q19;
            Q19=makeQuery(id+"F3.boolean.opBoolean","INTERSECT",EDGE,{"disambiguationData":[OD(1.0)],"derivedFrom":[makeQuery(id+"F1.opExtrude","SWEPT_FACE",FACE,{"disambiguationData":[OSD([sQuery(id+"F0.wireOp",EDGE,"E6")])]}),makeQuery(id+"F3.opExtrude","SWEPT_FACE",FACE,{"disambiguationData":[OSD([sQuery(id+"F2.wireOp",EDGE,"E11")])]})]});
            var Q20;
            {var subQ0=sQuery(id+"F0.wireOp",EDGE,"E6");var subQ1=makeQuery(id+"F1.opExtrude","SWEPT_FACE",FACE,{"disambiguationData":[OSD([subQ0])]});Q20=makeQuery(id+"F5.boolean.opBoolean","INTERSECT",EDGE,{"disambiguationData":[OD(0.0)],"derivedFrom":[makeQuery(id+"F3.boolean.opBoolean","SPLIT",FACE,{"disambiguationData":[TD([makeQuery(id+"F1.opExtrude","CAP_FACE",FACE,{"disambiguationData":[OSD([sQuery(id+"F0.wireOp",EDGE,"E0.bottom"),sQuery(id+"F0.wireOp",EDGE,"E0.left"),sQuery(id+"F0.wireOp",EDGE,"E1.bottom"),sQuery(id+"F0.wireOp",EDGE,"E1.top"),sQuery(id+"F0.wireOp",EDGE,"E1.left"),sQuery(id+"F0.wireOp",EDGE,"E2"),sQuery(id+"F0.wireOp",EDGE,"E3"),sQuery(id+"F0.wireOp",EDGE,"E4"),sQuery(id+"F0.wireOp",EDGE,"E5"),subQ0,sQuery(id+"F0.wireOp",EDGE,"E7"),sQuery(id+"F0.wireOp",EDGE,"E8")])],"isStart":false})])],"derivedFrom":subQ1}),makeQuery(id+"F5.opExtrude","SWEPT_FACE",FACE,{"disambiguationData":[OSD([sQuery(id+"F4.wireOp",EDGE,"E15")])]})]});}
            var Q21;
            {var subQ0=sQuery(id+"F0.wireOp",EDGE,"E6");var subQ1=makeQuery(id+"F1.opExtrude","SWEPT_FACE",FACE,{"disambiguationData":[OSD([subQ0])]});Q21=makeQuery(id+"F5.boolean.opBoolean","INTERSECT",EDGE,{"disambiguationData":[OD(0.0)],"derivedFrom":[makeQuery(id+"F3.boolean.opBoolean","SPLIT",FACE,{"disambiguationData":[TD([makeQuery(id+"F1.opExtrude","CAP_FACE",FACE,{"disambiguationData":[OSD([sQuery(id+"F0.wireOp",EDGE,"E0.bottom"),sQuery(id+"F0.wireOp",EDGE,"E0.left"),sQuery(id+"F0.wireOp",EDGE,"E1.bottom"),sQuery(id+"F0.wireOp",EDGE,"E1.top"),sQuery(id+"F0.wireOp",EDGE,"E1.left"),sQuery(id+"F0.wireOp",EDGE,"E2"),sQuery(id+"F0.wireOp",EDGE,"E3"),sQuery(id+"F0.wireOp",EDGE,"E4"),sQuery(id+"F0.wireOp",EDGE,"E5"),subQ0,sQuery(id+"F0.wireOp",EDGE,"E7"),sQuery(id+"F0.wireOp",EDGE,"E8")])],"isStart":true})])],"derivedFrom":subQ1}),makeQuery(id+"F5.opExtrude","SWEPT_FACE",FACE,{"disambiguationData":[OSD([sQuery(id+"F4.wireOp",EDGE,"E15")])]})]});}
            var Q22;
            Q22=makeQuery(id+"F5.boolean.opBoolean","INTERSECT",EDGE,{"disambiguationData":[OD(0.0)],"derivedFrom":[makeQuery(id+"F3.boolean.opBoolean","COPY",FACE,{"disambiguationData":[OD(2.0)],"derivedFrom":makeQuery(id+"F3.opExtrude","SWEPT_FACE",FACE,{"disambiguationData":[OSD([sQuery(id+"F2.wireOp",EDGE,"E11")])]})}),makeQuery(id+"F5.opExtrude","SWEPT_FACE",FACE,{"disambiguationData":[OSD([sQuery(id+"F4.wireOp",EDGE,"E15")])]})]});
            var Q23;
            Q23=makeQuery(id+"F5.boolean.opBoolean","INTERSECT",EDGE,{"disambiguationData":[OD(1.0)],"derivedFrom":[makeQuery(id+"F3.boolean.opBoolean","COPY",FACE,{"disambiguationData":[OD(0.0)],"derivedFrom":makeQuery(id+"F3.opExtrude","SWEPT_FACE",FACE,{"disambiguationData":[OSD([sQuery(id+"F2.wireOp",EDGE,"E11")])]})}),makeQuery(id+"F5.opExtrude","SWEPT_FACE",FACE,{"disambiguationData":[OSD([sQuery(id+"F4.wireOp",EDGE,"E15")])]})]});
            var Q24;
            Q24=makeQuery(id+"F3.boolean.opBoolean","INTERSECT",EDGE,{"disambiguationData":[OD(0.0)],"derivedFrom":[makeQuery(id+"F1.opExtrude","SWEPT_FACE",FACE,{"disambiguationData":[OSD([sQuery(id+"F0.wireOp",EDGE,"E7")])]}),makeQuery(id+"F3.opExtrude","SWEPT_FACE",FACE,{"disambiguationData":[OSD([sQuery(id+"F2.wireOp",EDGE,"E11")])]})]});
            var Q25;
            {var subQ0=sQuery(id+"F0.wireOp",EDGE,"E7");var subQ1=makeQuery(id+"F1.opExtrude","SWEPT_FACE",FACE,{"disambiguationData":[OSD([subQ0])]});Q25=makeQuery(id+"F5.boolean.opBoolean","INTERSECT",EDGE,{"disambiguationData":[OD(0.0)],"derivedFrom":[makeQuery(id+"F3.boolean.opBoolean","SPLIT",FACE,{"disambiguationData":[TD([makeQuery(id+"F1.opExtrude","CAP_FACE",FACE,{"disambiguationData":[OSD([sQuery(id+"F0.wireOp",EDGE,"E0.bottom"),sQuery(id+"F0.wireOp",EDGE,"E0.left"),sQuery(id+"F0.wireOp",EDGE,"E1.bottom"),sQuery(id+"F0.wireOp",EDGE,"E1.top"),sQuery(id+"F0.wireOp",EDGE,"E1.left"),sQuery(id+"F0.wireOp",EDGE,"E2"),sQuery(id+"F0.wireOp",EDGE,"E3"),sQuery(id+"F0.wireOp",EDGE,"E4"),sQuery(id+"F0.wireOp",EDGE,"E5"),sQuery(id+"F0.wireOp",EDGE,"E6"),subQ0,sQuery(id+"F0.wireOp",EDGE,"E8")])],"isStart":true})])],"derivedFrom":subQ1}),makeQuery(id+"F5.opExtrude","SWEPT_FACE",FACE,{"disambiguationData":[OSD([sQuery(id+"F4.wireOp",EDGE,"E16")])]})]});}
            var Q26;
            Q26=makeQuery(id+"F5.boolean.opBoolean","INTERSECT",EDGE,{"disambiguationData":[OD(0.0)],"derivedFrom":[makeQuery(id+"F3.boolean.opBoolean","COPY",FACE,{"disambiguationData":[OD(2.0)],"derivedFrom":makeQuery(id+"F3.opExtrude","SWEPT_FACE",FACE,{"disambiguationData":[OSD([sQuery(id+"F2.wireOp",EDGE,"E11")])]})}),makeQuery(id+"F5.opExtrude","SWEPT_FACE",FACE,{"disambiguationData":[OSD([sQuery(id+"F4.wireOp",EDGE,"E16")])]})]});
            var Q27;
            Q27=makeQuery(id+"F3.boolean.opBoolean","INTERSECT",EDGE,{"disambiguationData":[OD(2.0)],"derivedFrom":[makeQuery(id+"F1.opExtrude","SWEPT_FACE",FACE,{"disambiguationData":[OSD([sQuery(id+"F0.wireOp",EDGE,"E7")])]}),makeQuery(id+"F3.opExtrude","SWEPT_FACE",FACE,{"disambiguationData":[OSD([sQuery(id+"F2.wireOp",EDGE,"E11")])]})]});
            var Q28;
            {var subQ0=sQuery(id+"F0.wireOp",EDGE,"E7");var subQ1=makeQuery(id+"F1.opExtrude","SWEPT_FACE",FACE,{"disambiguationData":[OSD([subQ0])]});Q28=makeQuery(id+"F5.boolean.opBoolean","INTERSECT",EDGE,{"disambiguationData":[OD(0.0)],"derivedFrom":[makeQuery(id+"F3.boolean.opBoolean","SPLIT",FACE,{"disambiguationData":[TD([makeQuery(id+"F1.opExtrude","CAP_FACE",FACE,{"disambiguationData":[OSD([sQuery(id+"F0.wireOp",EDGE,"E0.bottom"),sQuery(id+"F0.wireOp",EDGE,"E0.left"),sQuery(id+"F0.wireOp",EDGE,"E1.bottom"),sQuery(id+"F0.wireOp",EDGE,"E1.top"),sQuery(id+"F0.wireOp",EDGE,"E1.left"),sQuery(id+"F0.wireOp",EDGE,"E2"),sQuery(id+"F0.wireOp",EDGE,"E3"),sQuery(id+"F0.wireOp",EDGE,"E4"),sQuery(id+"F0.wireOp",EDGE,"E5"),sQuery(id+"F0.wireOp",EDGE,"E6"),subQ0,sQuery(id+"F0.wireOp",EDGE,"E8")])],"isStart":false})])],"derivedFrom":subQ1}),makeQuery(id+"F5.opExtrude","SWEPT_FACE",FACE,{"disambiguationData":[OSD([sQuery(id+"F4.wireOp",EDGE,"E16")])]})]});}
            var Q29;
            Q29=makeQuery(id+"F5.boolean.opBoolean","INTERSECT",EDGE,{"disambiguationData":[OD(1.0)],"derivedFrom":[makeQuery(id+"F3.boolean.opBoolean","COPY",FACE,{"disambiguationData":[OD(2.0)],"derivedFrom":makeQuery(id+"F3.opExtrude","SWEPT_FACE",FACE,{"disambiguationData":[OSD([sQuery(id+"F2.wireOp",EDGE,"E11")])]})}),makeQuery(id+"F5.opExtrude","SWEPT_FACE",FACE,{"disambiguationData":[OSD([sQuery(id+"F4.wireOp",EDGE,"E16")])]})]});
            var Q30;
            {var subQ0=sQuery(id+"F0.wireOp",EDGE,"E7");var subQ1=makeQuery(id+"F1.opExtrude","SWEPT_FACE",FACE,{"disambiguationData":[OSD([subQ0])]});Q30=makeQuery(id+"F5.boolean.opBoolean","INTERSECT",EDGE,{"disambiguationData":[OD(1.0)],"derivedFrom":[makeQuery(id+"F3.boolean.opBoolean","SPLIT",FACE,{"disambiguationData":[TD([makeQuery(id+"F1.opExtrude","CAP_FACE",FACE,{"disambiguationData":[OSD([sQuery(id+"F0.wireOp",EDGE,"E0.bottom"),sQuery(id+"F0.wireOp",EDGE,"E0.left"),sQuery(id+"F0.wireOp",EDGE,"E1.bottom"),sQuery(id+"F0.wireOp",EDGE,"E1.top"),sQuery(id+"F0.wireOp",EDGE,"E1.left"),sQuery(id+"F0.wireOp",EDGE,"E2"),sQuery(id+"F0.wireOp",EDGE,"E3"),sQuery(id+"F0.wireOp",EDGE,"E4"),sQuery(id+"F0.wireOp",EDGE,"E5"),sQuery(id+"F0.wireOp",EDGE,"E6"),subQ0,sQuery(id+"F0.wireOp",EDGE,"E8")])],"isStart":true})])],"derivedFrom":subQ1}),makeQuery(id+"F5.opExtrude","SWEPT_FACE",FACE,{"disambiguationData":[OSD([sQuery(id+"F4.wireOp",EDGE,"E16")])]})]});}
            var Q31;
            {var subQ0=sQuery(id+"F0.wireOp",EDGE,"E7");var subQ1=makeQuery(id+"F1.opExtrude","SWEPT_FACE",FACE,{"disambiguationData":[OSD([subQ0])]});Q31=makeQuery(id+"F5.boolean.opBoolean","INTERSECT",EDGE,{"disambiguationData":[OD(1.0)],"derivedFrom":[makeQuery(id+"F3.boolean.opBoolean","SPLIT",FACE,{"disambiguationData":[TD([makeQuery(id+"F1.opExtrude","CAP_FACE",FACE,{"disambiguationData":[OSD([sQuery(id+"F0.wireOp",EDGE,"E0.bottom"),sQuery(id+"F0.wireOp",EDGE,"E0.left"),sQuery(id+"F0.wireOp",EDGE,"E1.bottom"),sQuery(id+"F0.wireOp",EDGE,"E1.top"),sQuery(id+"F0.wireOp",EDGE,"E1.left"),sQuery(id+"F0.wireOp",EDGE,"E2"),sQuery(id+"F0.wireOp",EDGE,"E3"),sQuery(id+"F0.wireOp",EDGE,"E4"),sQuery(id+"F0.wireOp",EDGE,"E5"),sQuery(id+"F0.wireOp",EDGE,"E6"),subQ0,sQuery(id+"F0.wireOp",EDGE,"E8")])],"isStart":false})])],"derivedFrom":subQ1}),makeQuery(id+"F5.opExtrude","SWEPT_FACE",FACE,{"disambiguationData":[OSD([sQuery(id+"F4.wireOp",EDGE,"E16")])]})]});}
            var Q32;
            Q32=makeQuery(id+"F5.boolean.opBoolean","INTERSECT",EDGE,{"disambiguationData":[OD(1.0)],"derivedFrom":[makeQuery(id+"F3.boolean.opBoolean","COPY",FACE,{"disambiguationData":[OD(3.0)],"derivedFrom":makeQuery(id+"F3.opExtrude","SWEPT_FACE",FACE,{"disambiguationData":[OSD([sQuery(id+"F2.wireOp",EDGE,"E11")])]})}),makeQuery(id+"F5.opExtrude","SWEPT_FACE",FACE,{"disambiguationData":[OSD([sQuery(id+"F4.wireOp",EDGE,"E16")])]})]});
            var Q33;
            Q33=makeQuery(id+"F3.boolean.opBoolean","INTERSECT",EDGE,{"disambiguationData":[OD(1.0)],"derivedFrom":[makeQuery(id+"F1.opExtrude","SWEPT_FACE",FACE,{"disambiguationData":[OSD([sQuery(id+"F0.wireOp",EDGE,"E7")])]}),makeQuery(id+"F3.opExtrude","SWEPT_FACE",FACE,{"disambiguationData":[OSD([sQuery(id+"F2.wireOp",EDGE,"E11")])]})]});
            var Q34;
            Q34=makeQuery(id+"F5.boolean.opBoolean","INTERSECT",EDGE,{"disambiguationData":[OD(0.0)],"derivedFrom":[makeQuery(id+"F3.boolean.opBoolean","COPY",FACE,{"disambiguationData":[OD(3.0)],"derivedFrom":makeQuery(id+"F3.opExtrude","SWEPT_FACE",FACE,{"disambiguationData":[OSD([sQuery(id+"F2.wireOp",EDGE,"E11")])]})}),makeQuery(id+"F5.opExtrude","SWEPT_FACE",FACE,{"disambiguationData":[OSD([sQuery(id+"F4.wireOp",EDGE,"E16")])]})]});
            var Q35;
            Q35=makeQuery(id+"F3.boolean.opBoolean","INTERSECT",EDGE,{"disambiguationData":[OD(3.0)],"derivedFrom":[makeQuery(id+"F1.opExtrude","SWEPT_FACE",FACE,{"disambiguationData":[OSD([sQuery(id+"F0.wireOp",EDGE,"E7")])]}),makeQuery(id+"F3.opExtrude","SWEPT_FACE",FACE,{"disambiguationData":[OSD([sQuery(id+"F2.wireOp",EDGE,"E11")])]})]});
            var Q36;
            Q36=makeQuery(id+"F5.boolean.opBoolean","INTERSECT",EDGE,{"disambiguationData":[OD(1.0)],"derivedFrom":[makeQuery(id+"F3.boolean.opBoolean","COPY",FACE,{"disambiguationData":[OD(3.0)],"derivedFrom":makeQuery(id+"F3.opExtrude","SWEPT_FACE",FACE,{"disambiguationData":[OSD([sQuery(id+"F2.wireOp",EDGE,"E11")])]})}),makeQuery(id+"F5.opExtrude","SWEPT_FACE",FACE,{"disambiguationData":[OSD([sQuery(id+"F4.wireOp",EDGE,"E17")])]})]});
            var Q37;
            {var subQ0=sQuery(id+"F0.wireOp",EDGE,"E8");var subQ1=makeQuery(id+"F1.opExtrude","SWEPT_FACE",FACE,{"disambiguationData":[OSD([subQ0])]});Q37=makeQuery(id+"F5.boolean.opBoolean","INTERSECT",EDGE,{"disambiguationData":[OD(1.0)],"derivedFrom":[makeQuery(id+"F3.boolean.opBoolean","SPLIT",FACE,{"disambiguationData":[TD([makeQuery(id+"F1.opExtrude","CAP_FACE",FACE,{"disambiguationData":[OSD([sQuery(id+"F0.wireOp",EDGE,"E0.bottom"),sQuery(id+"F0.wireOp",EDGE,"E0.left"),sQuery(id+"F0.wireOp",EDGE,"E1.bottom"),sQuery(id+"F0.wireOp",EDGE,"E1.top"),sQuery(id+"F0.wireOp",EDGE,"E1.left"),sQuery(id+"F0.wireOp",EDGE,"E2"),sQuery(id+"F0.wireOp",EDGE,"E3"),sQuery(id+"F0.wireOp",EDGE,"E4"),sQuery(id+"F0.wireOp",EDGE,"E5"),sQuery(id+"F0.wireOp",EDGE,"E6"),sQuery(id+"F0.wireOp",EDGE,"E7"),subQ0])],"isStart":false})])],"derivedFrom":subQ1}),makeQuery(id+"F5.opExtrude","SWEPT_FACE",FACE,{"disambiguationData":[OSD([sQuery(id+"F4.wireOp",EDGE,"E17")])]})]});}
            var Q38;
            Q38=makeQuery(id+"F3.boolean.opBoolean","INTERSECT",EDGE,{"disambiguationData":[OD(3.0)],"derivedFrom":[makeQuery(id+"F1.opExtrude","SWEPT_FACE",FACE,{"disambiguationData":[OSD([sQuery(id+"F0.wireOp",EDGE,"E8")])]}),makeQuery(id+"F3.opExtrude","SWEPT_FACE",FACE,{"disambiguationData":[OSD([sQuery(id+"F2.wireOp",EDGE,"E11")])]})]});
            var Q39;
            Q39=makeQuery(id+"F3.boolean.opBoolean","INTERSECT",EDGE,{"disambiguationData":[OD(2.0)],"derivedFrom":[makeQuery(id+"F1.opExtrude","SWEPT_FACE",FACE,{"disambiguationData":[OSD([sQuery(id+"F0.wireOp",EDGE,"E8")])]}),makeQuery(id+"F3.opExtrude","SWEPT_FACE",FACE,{"disambiguationData":[OSD([sQuery(id+"F2.wireOp",EDGE,"E11")])]})]});
            var Q40;
            {var subQ0=sQuery(id+"F0.wireOp",EDGE,"E8");var subQ1=makeQuery(id+"F1.opExtrude","SWEPT_FACE",FACE,{"disambiguationData":[OSD([subQ0])]});Q40=makeQuery(id+"F5.boolean.opBoolean","INTERSECT",EDGE,{"disambiguationData":[OD(1.0)],"derivedFrom":[makeQuery(id+"F3.boolean.opBoolean","SPLIT",FACE,{"disambiguationData":[TD([makeQuery(id+"F1.opExtrude","CAP_FACE",FACE,{"disambiguationData":[OSD([sQuery(id+"F0.wireOp",EDGE,"E0.bottom"),sQuery(id+"F0.wireOp",EDGE,"E0.left"),sQuery(id+"F0.wireOp",EDGE,"E1.bottom"),sQuery(id+"F0.wireOp",EDGE,"E1.top"),sQuery(id+"F0.wireOp",EDGE,"E1.left"),sQuery(id+"F0.wireOp",EDGE,"E2"),sQuery(id+"F0.wireOp",EDGE,"E3"),sQuery(id+"F0.wireOp",EDGE,"E4"),sQuery(id+"F0.wireOp",EDGE,"E5"),sQuery(id+"F0.wireOp",EDGE,"E6"),sQuery(id+"F0.wireOp",EDGE,"E7"),subQ0])],"isStart":true})])],"derivedFrom":subQ1}),makeQuery(id+"F5.opExtrude","SWEPT_FACE",FACE,{"disambiguationData":[OSD([sQuery(id+"F4.wireOp",EDGE,"E17")])]})]});}
            var Q41;
            Q41=makeQuery(id+"F3.boolean.opBoolean","INTERSECT",EDGE,{"disambiguationData":[OD(0.0)],"derivedFrom":[makeQuery(id+"F1.opExtrude","SWEPT_FACE",FACE,{"disambiguationData":[OSD([sQuery(id+"F0.wireOp",EDGE,"E8")])]}),makeQuery(id+"F3.opExtrude","SWEPT_FACE",FACE,{"disambiguationData":[OSD([sQuery(id+"F2.wireOp",EDGE,"E11")])]})]});
            var Q42;
            {var subQ0=sQuery(id+"F0.wireOp",EDGE,"E8");var subQ1=makeQuery(id+"F1.opExtrude","SWEPT_FACE",FACE,{"disambiguationData":[OSD([subQ0])]});Q42=makeQuery(id+"F5.boolean.opBoolean","INTERSECT",EDGE,{"disambiguationData":[OD(0.0)],"derivedFrom":[makeQuery(id+"F3.boolean.opBoolean","SPLIT",FACE,{"disambiguationData":[TD([makeQuery(id+"F1.opExtrude","CAP_FACE",FACE,{"disambiguationData":[OSD([sQuery(id+"F0.wireOp",EDGE,"E0.bottom"),sQuery(id+"F0.wireOp",EDGE,"E0.left"),sQuery(id+"F0.wireOp",EDGE,"E1.bottom"),sQuery(id+"F0.wireOp",EDGE,"E1.top"),sQuery(id+"F0.wireOp",EDGE,"E1.left"),sQuery(id+"F0.wireOp",EDGE,"E2"),sQuery(id+"F0.wireOp",EDGE,"E3"),sQuery(id+"F0.wireOp",EDGE,"E4"),sQuery(id+"F0.wireOp",EDGE,"E5"),sQuery(id+"F0.wireOp",EDGE,"E6"),sQuery(id+"F0.wireOp",EDGE,"E7"),subQ0])],"isStart":true})])],"derivedFrom":subQ1}),makeQuery(id+"F5.opExtrude","SWEPT_FACE",FACE,{"disambiguationData":[OSD([sQuery(id+"F4.wireOp",EDGE,"E17")])]})]});}
            var Q43;
            Q43=makeQuery(id+"F5.boolean.opBoolean","INTERSECT",EDGE,{"disambiguationData":[OD(0.0)],"derivedFrom":[makeQuery(id+"F3.boolean.opBoolean","COPY",FACE,{"disambiguationData":[OD(3.0)],"derivedFrom":makeQuery(id+"F3.opExtrude","SWEPT_FACE",FACE,{"disambiguationData":[OSD([sQuery(id+"F2.wireOp",EDGE,"E11")])]})}),makeQuery(id+"F5.opExtrude","SWEPT_FACE",FACE,{"disambiguationData":[OSD([sQuery(id+"F4.wireOp",EDGE,"E17")])]})]});
            var Q44;
            Q44=makeQuery(id+"F5.boolean.opBoolean","INTERSECT",EDGE,{"disambiguationData":[OD(1.0)],"derivedFrom":[makeQuery(id+"F3.boolean.opBoolean","COPY",FACE,{"disambiguationData":[OD(1.0)],"derivedFrom":makeQuery(id+"F3.opExtrude","SWEPT_FACE",FACE,{"disambiguationData":[OSD([sQuery(id+"F2.wireOp",EDGE,"E11")])]})}),makeQuery(id+"F5.opExtrude","SWEPT_FACE",FACE,{"disambiguationData":[OSD([sQuery(id+"F4.wireOp",EDGE,"E17")])]})]});
            var Q45;
            Q45=makeQuery(id+"F5.boolean.opBoolean","INTERSECT",EDGE,{"disambiguationData":[OD(0.0)],"derivedFrom":[makeQuery(id+"F3.boolean.opBoolean","COPY",FACE,{"disambiguationData":[OD(1.0)],"derivedFrom":makeQuery(id+"F3.opExtrude","SWEPT_FACE",FACE,{"disambiguationData":[OSD([sQuery(id+"F2.wireOp",EDGE,"E11")])]})}),makeQuery(id+"F5.opExtrude","SWEPT_FACE",FACE,{"disambiguationData":[OSD([sQuery(id+"F4.wireOp",EDGE,"E17")])]})]});
            var Q46;
            Q46=makeQuery(id+"F3.boolean.opBoolean","INTERSECT",EDGE,{"disambiguationData":[OD(1.0)],"derivedFrom":[makeQuery(id+"F1.opExtrude","SWEPT_FACE",FACE,{"disambiguationData":[OSD([sQuery(id+"F0.wireOp",EDGE,"E8")])]}),makeQuery(id+"F3.opExtrude","SWEPT_FACE",FACE,{"disambiguationData":[OSD([sQuery(id+"F2.wireOp",EDGE,"E11")])]})]});
            var Q47;
            {var subQ0=sQuery(id+"F0.wireOp",EDGE,"E8");var subQ1=makeQuery(id+"F1.opExtrude","SWEPT_FACE",FACE,{"disambiguationData":[OSD([subQ0])]});Q47=makeQuery(id+"F5.boolean.opBoolean","INTERSECT",EDGE,{"disambiguationData":[OD(0.0)],"derivedFrom":[makeQuery(id+"F3.boolean.opBoolean","SPLIT",FACE,{"disambiguationData":[TD([makeQuery(id+"F1.opExtrude","CAP_FACE",FACE,{"disambiguationData":[OSD([sQuery(id+"F0.wireOp",EDGE,"E0.bottom"),sQuery(id+"F0.wireOp",EDGE,"E0.left"),sQuery(id+"F0.wireOp",EDGE,"E1.bottom"),sQuery(id+"F0.wireOp",EDGE,"E1.top"),sQuery(id+"F0.wireOp",EDGE,"E1.left"),sQuery(id+"F0.wireOp",EDGE,"E2"),sQuery(id+"F0.wireOp",EDGE,"E3"),sQuery(id+"F0.wireOp",EDGE,"E4"),sQuery(id+"F0.wireOp",EDGE,"E5"),sQuery(id+"F0.wireOp",EDGE,"E6"),sQuery(id+"F0.wireOp",EDGE,"E7"),subQ0])],"isStart":false})])],"derivedFrom":subQ1}),makeQuery(id+"F5.opExtrude","SWEPT_FACE",FACE,{"disambiguationData":[OSD([sQuery(id+"F4.wireOp",EDGE,"E17")])]})]});}
            fillet(context, id + "F8", {"entities" : qUnion([Q0, Q1, Q2, Q3, Q4, Q5, Q6, Q7, Q8, Q9, Q10, Q11, Q12, Q13, Q14, Q15, Q16, Q17, Q18, Q19, Q20, Q21, Q22, Q23, Q24, Q25, Q26, Q27, Q28, Q29, Q30, Q31, Q32, Q33, Q34, Q35, Q36, Q37, Q38, Q39, Q40, Q41, Q42, Q43, Q44, Q45, Q46, Q47]), "radius" : 2.54 * mm, "tangentPropagation" : true, "allowEdgeOverflow" : false});
        }
        {
            var Q0;
            Q0=makeQuery(id+"F1.opExtrude","CAP_EDGE",EDGE,{"disambiguationData":[OSD([sQuery(id+"F0.wireOp",EDGE,"E6")])],"isStart":false});
            var Q1;
            Q1=makeQuery(id+"F1.opExtrude","CAP_EDGE",EDGE,{"disambiguationData":[OSD([sQuery(id+"F0.wireOp",EDGE,"E5")])],"isStart":false});
            var Q2;
            Q2=makeQuery(id+"F1.opExtrude","CAP_EDGE",EDGE,{"disambiguationData":[OSD([sQuery(id+"F0.wireOp",EDGE,"E4")])],"isStart":false});
            var Q3;
            Q3=makeQuery(id+"F1.opExtrude","CAP_EDGE",EDGE,{"disambiguationData":[OSD([sQuery(id+"F0.wireOp",EDGE,"E7")])],"isStart":false});
            var Q4;
            Q4=makeQuery(id+"F1.opExtrude","CAP_EDGE",EDGE,{"disambiguationData":[OSD([sQuery(id+"F0.wireOp",EDGE,"E8")])],"isStart":false});
            var Q5;
            Q5=makeQuery(id+"F3.boolean.opBoolean","COPY",EDGE,{"derivedFrom":makeQuery(id+"F3.opExtrude","CAP_EDGE",EDGE,{"disambiguationData":[OSD([sQuery(id+"F2.wireOp",EDGE,"E11")])],"isStart":false})});
            var Q6;
            Q6=makeQuery(id+"F3.boolean.opBoolean","INTERSECT",EDGE,{"derivedFrom":[makeQuery(id+"F1.opExtrude","SWEPT_FACE",FACE,{"disambiguationData":[OSD([sQuery(id+"F0.wireOp",EDGE,"E3")])]}),makeQuery(id+"F3.opExtrude","SWEPT_FACE",FACE,{"disambiguationData":[OSD([sQuery(id+"F2.wireOp",EDGE,"E10")])]})]});
            var Q7;
            Q7=makeQuery(id+"F3.boolean.opBoolean","INTERSECT",EDGE,{"derivedFrom":[makeQuery(id+"F1.opExtrude","SWEPT_FACE",FACE,{"disambiguationData":[OSD([sQuery(id+"F0.wireOp",EDGE,"E3")])]}),makeQuery(id+"F3.opExtrude","SWEPT_FACE",FACE,{"disambiguationData":[OSD([sQuery(id+"F2.wireOp",EDGE,"E9")])]})]});
            var Q8;
            Q8=makeQuery(id+"F5.boolean.opBoolean","INTERSECT",EDGE,{"derivedFrom":[makeQuery(id+"F1.opExtrude","SWEPT_FACE",FACE,{"disambiguationData":[OSD([sQuery(id+"F0.wireOp",EDGE,"E2")])]}),makeQuery(id+"F5.opExtrude","SWEPT_FACE",FACE,{"disambiguationData":[OSD([sQuery(id+"F4.wireOp",EDGE,"E17")])]})]});
            var Q9;
            Q9=makeQuery(id+"F5.boolean.opBoolean","INTERSECT",EDGE,{"derivedFrom":[makeQuery(id+"F1.opExtrude","SWEPT_FACE",FACE,{"disambiguationData":[OSD([sQuery(id+"F0.wireOp",EDGE,"E2")])]}),makeQuery(id+"F5.opExtrude","SWEPT_FACE",FACE,{"disambiguationData":[OSD([sQuery(id+"F4.wireOp",EDGE,"E16")])]})]});
            var Q10;
            Q10=makeQuery(id+"F5.boolean.opBoolean","COPY",EDGE,{"derivedFrom":makeQuery(id+"F5.opExtrude","CAP_EDGE",EDGE,{"disambiguationData":[OSD([sQuery(id+"F4.wireOp",EDGE,"E15")])],"isStart":false})});
            var Q11;
            Q11=makeQuery(id+"F1.opExtrude","CAP_EDGE",EDGE,{"disambiguationData":[OSD([sQuery(id+"F0.wireOp",EDGE,"E4")])],"isStart":true});
            var Q12;
            Q12=makeQuery(id+"F1.opExtrude","CAP_EDGE",EDGE,{"disambiguationData":[OSD([sQuery(id+"F0.wireOp",EDGE,"E5")])],"isStart":true});
            var Q13;
            Q13=makeQuery(id+"F1.opExtrude","CAP_EDGE",EDGE,{"disambiguationData":[OSD([sQuery(id+"F0.wireOp",EDGE,"E6")])],"isStart":true});
            var Q14;
            Q14=makeQuery(id+"F1.opExtrude","CAP_EDGE",EDGE,{"disambiguationData":[OSD([sQuery(id+"F0.wireOp",EDGE,"E7")])],"isStart":true});
            var Q15;
            Q15=makeQuery(id+"F1.opExtrude","CAP_EDGE",EDGE,{"disambiguationData":[OSD([sQuery(id+"F0.wireOp",EDGE,"E8")])],"isStart":true});
            var Q16;
            Q16=makeQuery(id+"F3.boolean.opBoolean","COPY",EDGE,{"derivedFrom":makeQuery(id+"F3.opExtrude","CAP_EDGE",EDGE,{"disambiguationData":[OSD([sQuery(id+"F2.wireOp",EDGE,"E11")])],"isStart":true})});
            var Q17;
            Q17=makeQuery(id+"F3.boolean.opBoolean","COPY",EDGE,{"derivedFrom":makeQuery(id+"F3.opExtrude","CAP_EDGE",EDGE,{"disambiguationData":[OSD([sQuery(id+"F2.wireOp",EDGE,"E10")])],"isStart":true})});
            var Q18;
            Q18=makeQuery(id+"F3.boolean.opBoolean","COPY",EDGE,{"derivedFrom":makeQuery(id+"F3.opExtrude","CAP_EDGE",EDGE,{"disambiguationData":[OSD([sQuery(id+"F2.wireOp",EDGE,"E9")])],"isStart":true})});
            var Q19;
            Q19=makeQuery(id+"F5.boolean.opBoolean","COPY",EDGE,{"derivedFrom":makeQuery(id+"F5.opExtrude","CAP_EDGE",EDGE,{"disambiguationData":[OSD([sQuery(id+"F4.wireOp",EDGE,"E15")])],"isStart":true})});
            var Q20;
            Q20=makeQuery(id+"F5.boolean.opBoolean","COPY",EDGE,{"derivedFrom":makeQuery(id+"F5.opExtrude","CAP_EDGE",EDGE,{"disambiguationData":[OSD([sQuery(id+"F4.wireOp",EDGE,"E16")])],"isStart":true})});
            var Q21;
            Q21=makeQuery(id+"F5.boolean.opBoolean","COPY",EDGE,{"derivedFrom":makeQuery(id+"F5.opExtrude","CAP_EDGE",EDGE,{"disambiguationData":[OSD([sQuery(id+"F4.wireOp",EDGE,"E17")])],"isStart":true})});
            fillet(context, id + "F9", {"entities" : qUnion([Q0, Q1, Q2, Q3, Q4, Q5, Q6, Q7, Q8, Q9, Q10, Q11, Q12, Q13, Q14, Q15, Q16, Q17, Q18, Q19, Q20, Q21]), "radius" : 2.54 * mm, "tangentPropagation" : true, "allowEdgeOverflow" : false});
        }
    });
